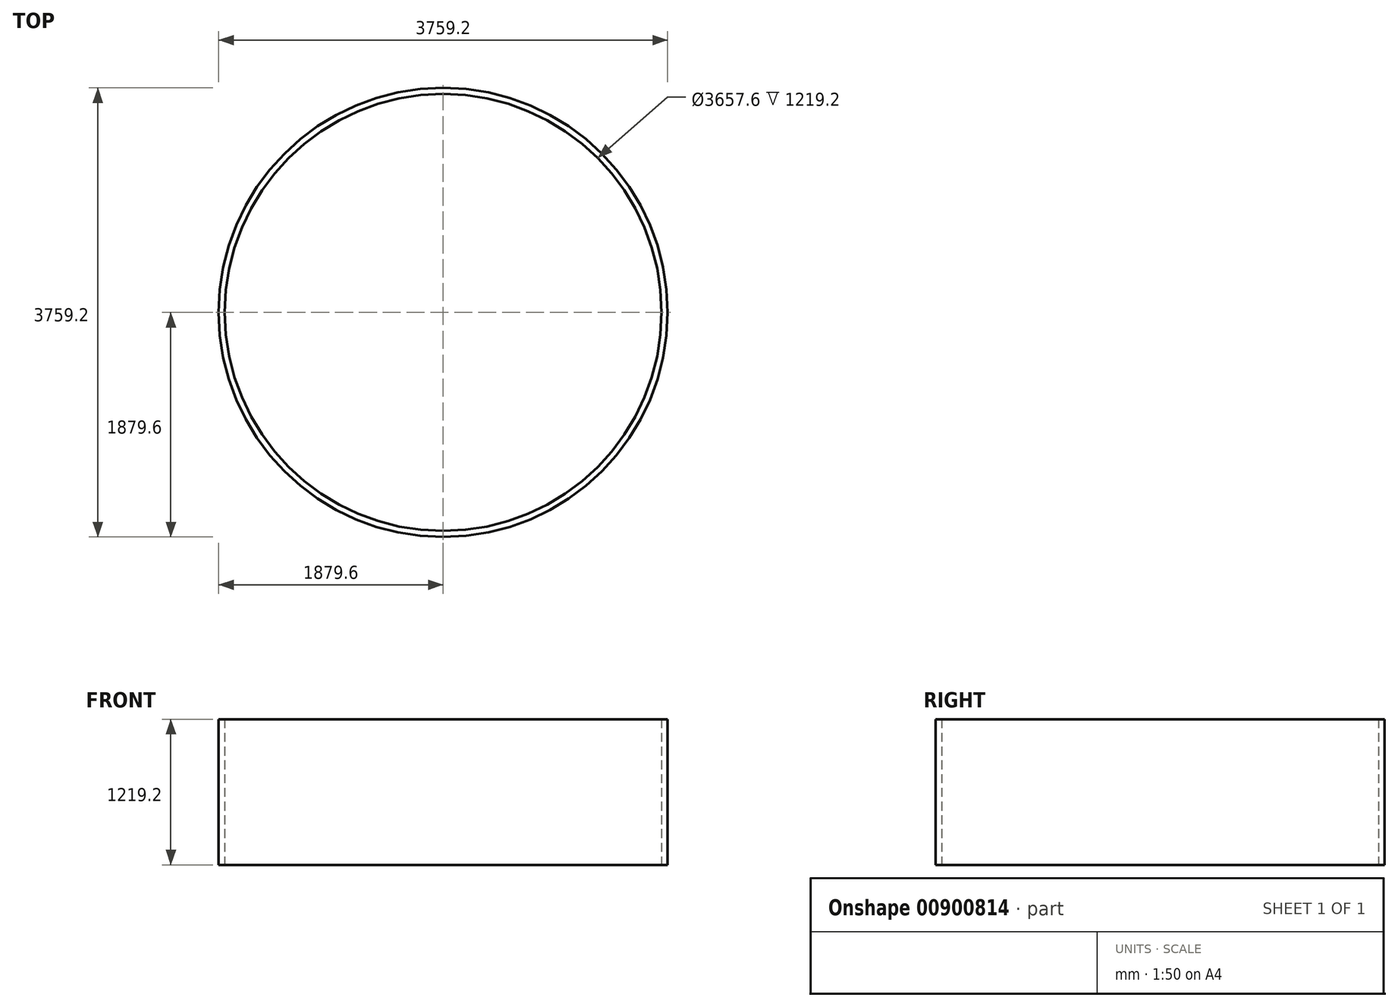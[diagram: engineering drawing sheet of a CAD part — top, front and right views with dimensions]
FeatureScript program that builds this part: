
annotation { "Feature Type Name" : "Feature", "Feature Type Description" : "" }
export const myFeature = defineFeature(function(context is Context, id is Id, definition is map)
    precondition{}
    {
        {
            var Q0;
            Q0=qCreatedBy(makeId("Top.planeOp"),FACE);
            var sketch = newSketch(context, id + "F0", { "sketchPlane" : qUnion([Q0])});
            skCircle(sketch, "E0", {"center": v(0, 0) * mm, "radius": 1828.8 * mm});
            skCircle(sketch, "E1", {"center": v(0, 0) * mm, "radius": 1879.6 * mm});
            skSolve(sketch);
        }
        {
            var Q0;
            Q0 = qSketchRegion(id + "F0", true);
            extrude(context, id + "F1", {"entities" : qUnion([Q0]), "depth" : 1219.2 * mm, "offsetDistance" : 25.4 * mm});
        }
    });
